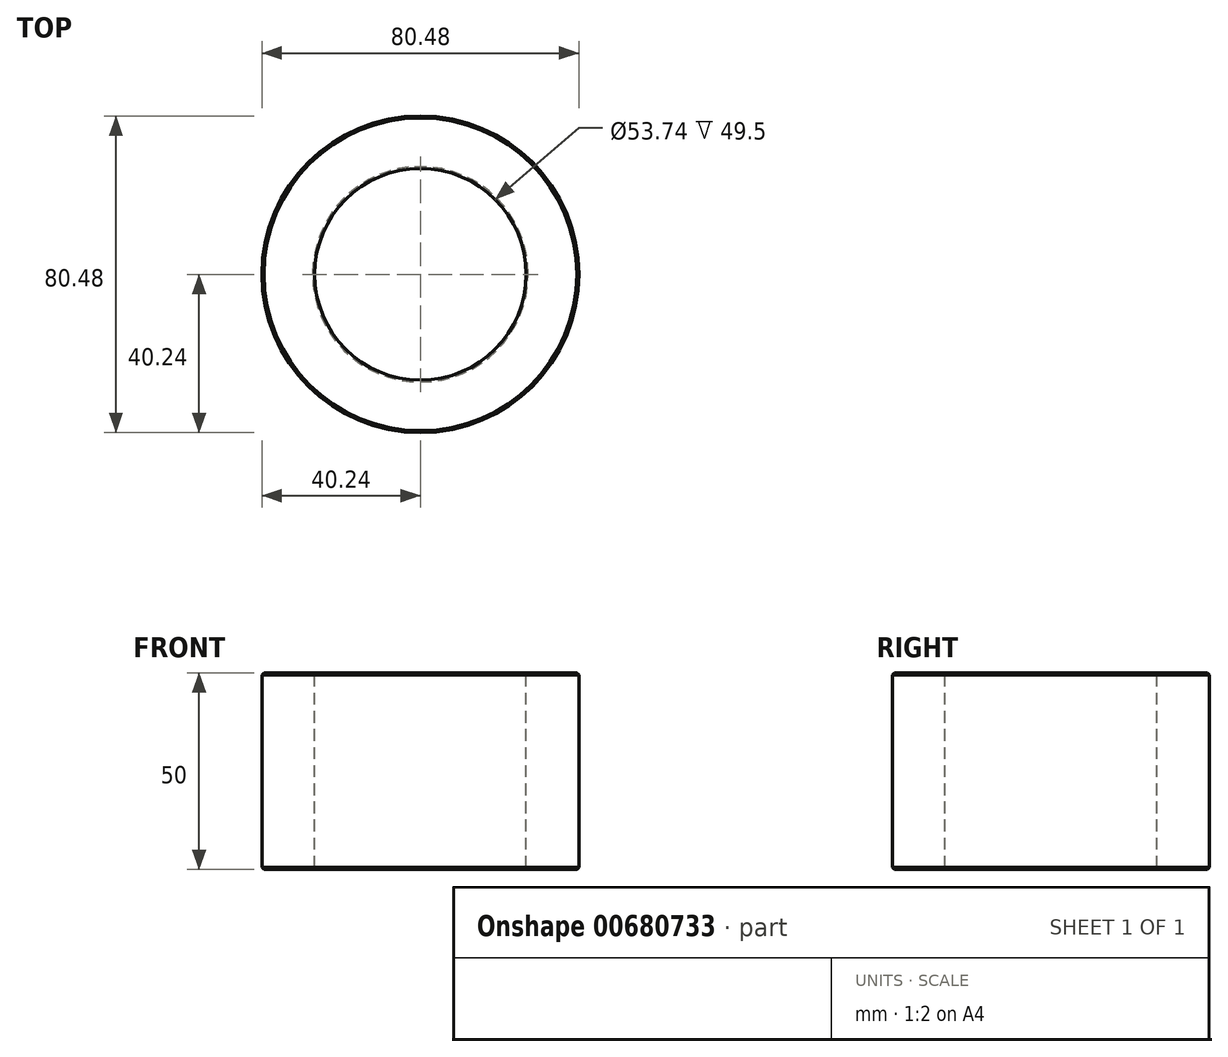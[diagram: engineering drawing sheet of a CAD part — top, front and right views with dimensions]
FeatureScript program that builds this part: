
annotation { "Feature Type Name" : "Feature", "Feature Type Description" : "" }
export const myFeature = defineFeature(function(context is Context, id is Id, definition is map)
    precondition{}
    {
        {
            var Q0;
            Q0=qCreatedBy(makeId("Top.planeOp"),FACE);
            var sketch = newSketch(context, id + "F0", { "sketchPlane" : qUnion([Q0])});
            skCircle(sketch, "E0", {"center": v(0, 0) * mm, "radius": 40.24 * mm});
            skSolve(sketch);
        }
        {
            var Q0;
            Q0=makeQuery(id+"F0.imprint","IMPRINT",FACE,{"disambiguationData":[TD([[makeQuery(id+"F0.imprint","IMPRINT",EDGE,{"derivedFrom":sQuery(id+"F0.wireOp",EDGE,"E0")}),1.0]])]});
            var Q1;
            Q1=qSketchRegion(id+"F0",true);
            extrude(context, id + "F1", {"entities" : qUnion([Q0, Q1]), "depth" : 50 * mm, "offsetDistance" : 25.4 * mm});
        }
        {
            var Q0;
            Q0=makeQuery(id+"F1.opExtrude","CAP_FACE",FACE,{"disambiguationData":[OSD([sQuery(id+"F0.wireOp",EDGE,"E0")])],"isStart":false});
            var sketch = newSketch(context, id + "F2", { "sketchPlane" : qUnion([Q0])});
            skCircle(sketch, "E1", {"center": v(0, 0) * mm, "radius": 26.87 * mm});
            skSolve(sketch);
        }
        {
            var Q0;
            Q0=makeQuery(id+"F2.imprint","IMPRINT",FACE,{"disambiguationData":[TD([[makeQuery(id+"F2.imprint","IMPRINT",EDGE,{"derivedFrom":sQuery(id+"F2.wireOp",EDGE,"E1")}),1.0]])]});
            extrude(context, id + "F3", {"entities" : qUnion([Q0]), "operationType" : NewBodyOperationType.REMOVE, "oppositeDirection" : true, "depth" : 62 * mm, "offsetDistance" : 25.4 * mm});
        }
        {
            var Q0;
            Q0=makeQuery(id+"F1.opExtrude","CAP_EDGE",EDGE,{"disambiguationData":[OSD([sQuery(id+"F0.wireOp",EDGE,"E0")])],"isStart":false});
            var Q1;
            Q1=makeQuery(id+"F3.boolean.opBoolean","COPY",EDGE,{"derivedFrom":makeQuery(id+"F3.opExtrude","CAP_EDGE",EDGE,{"disambiguationData":[OSD([sQuery(id+"F2.wireOp",EDGE,"E1")])],"isStart":true})});
            var Q2;
            Q2=makeQuery(id+"F1.opExtrude","CAP_EDGE",EDGE,{"disambiguationData":[OSD([sQuery(id+"F0.wireOp",EDGE,"E0")])],"isStart":true});
            var Q3;
            Q3=makeQuery(id+"F3.boolean.opBoolean","INTERSECT",EDGE,{"derivedFrom":[makeQuery(id+"F1.opExtrude","CAP_FACE",FACE,{"disambiguationData":[OSD([sQuery(id+"F0.wireOp",EDGE,"E0")])],"isStart":true}),makeQuery(id+"F3.opExtrude","SWEPT_FACE",FACE,{"disambiguationData":[OSD([sQuery(id+"F2.wireOp",EDGE,"E1")])]})]});
            chamfer(context, id + "F4", {"entities" : qUnion([Q0, Q1, Q2, Q3]), "width" : 0.5 * mm, "tangentPropagation" : true});
        }
    });
